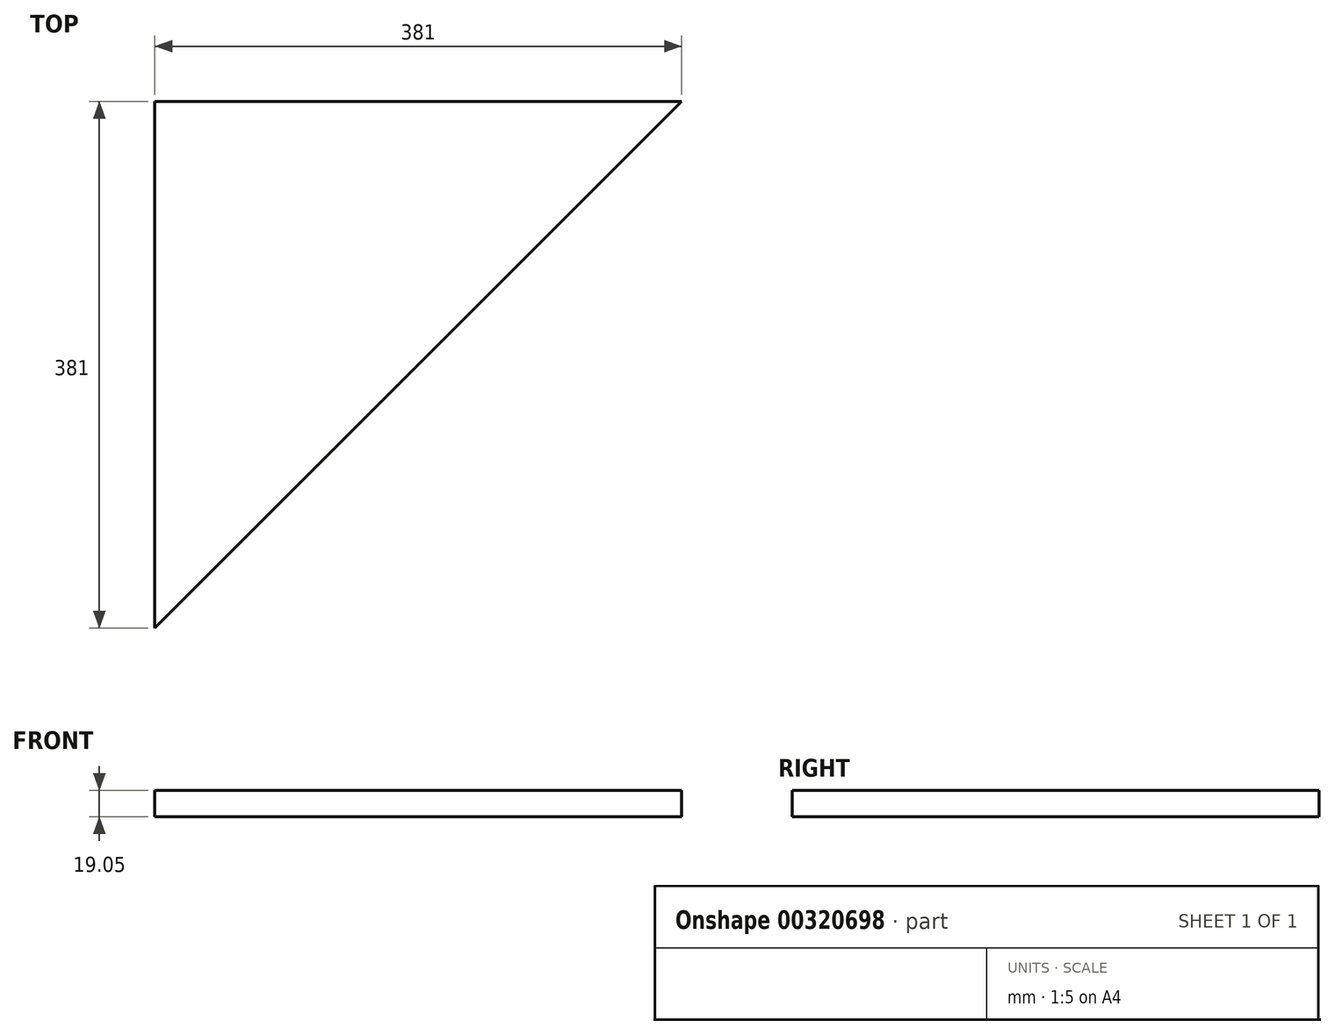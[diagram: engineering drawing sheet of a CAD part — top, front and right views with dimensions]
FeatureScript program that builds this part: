
annotation { "Feature Type Name" : "Feature", "Feature Type Description" : "" }
export const myFeature = defineFeature(function(context is Context, id is Id, definition is map)
    precondition{}
    {
        {
            var Q0;
            Q0=qCreatedBy(makeId("Top.planeOp"),FACE);
            var sketch = newSketch(context, id + "F0", { "sketchPlane" : qUnion([Q0])});
            skLineSegment(sketch, "E0", {"start": v(-36.52, 201.3) * mm, "end": v(-36.52, -179.7) * mm});
            skLineSegment(sketch, "E1", {"start": v(-36.52, 201.3) * mm, "end": v(344.48, 201.3) * mm});
            skLineSegment(sketch, "E2", {"start": v(344.48, 201.3) * mm, "end": v(-36.52, -179.7) * mm});
            skSolve(sketch);
        }
        {
            var Q0;
            Q0=makeQuery(id+"F0.imprint","IMPRINT",FACE,{"disambiguationData":[TD([[makeQuery(id+"F0.imprint","IMPRINT",EDGE,{"derivedFrom":sQuery(id+"F0.wireOp",EDGE,"E0")}),1.0]])]});
            extrude(context, id + "F1", {"entities" : qUnion([Q0]), "depth" : 19.05 * mm});
        }
    });
